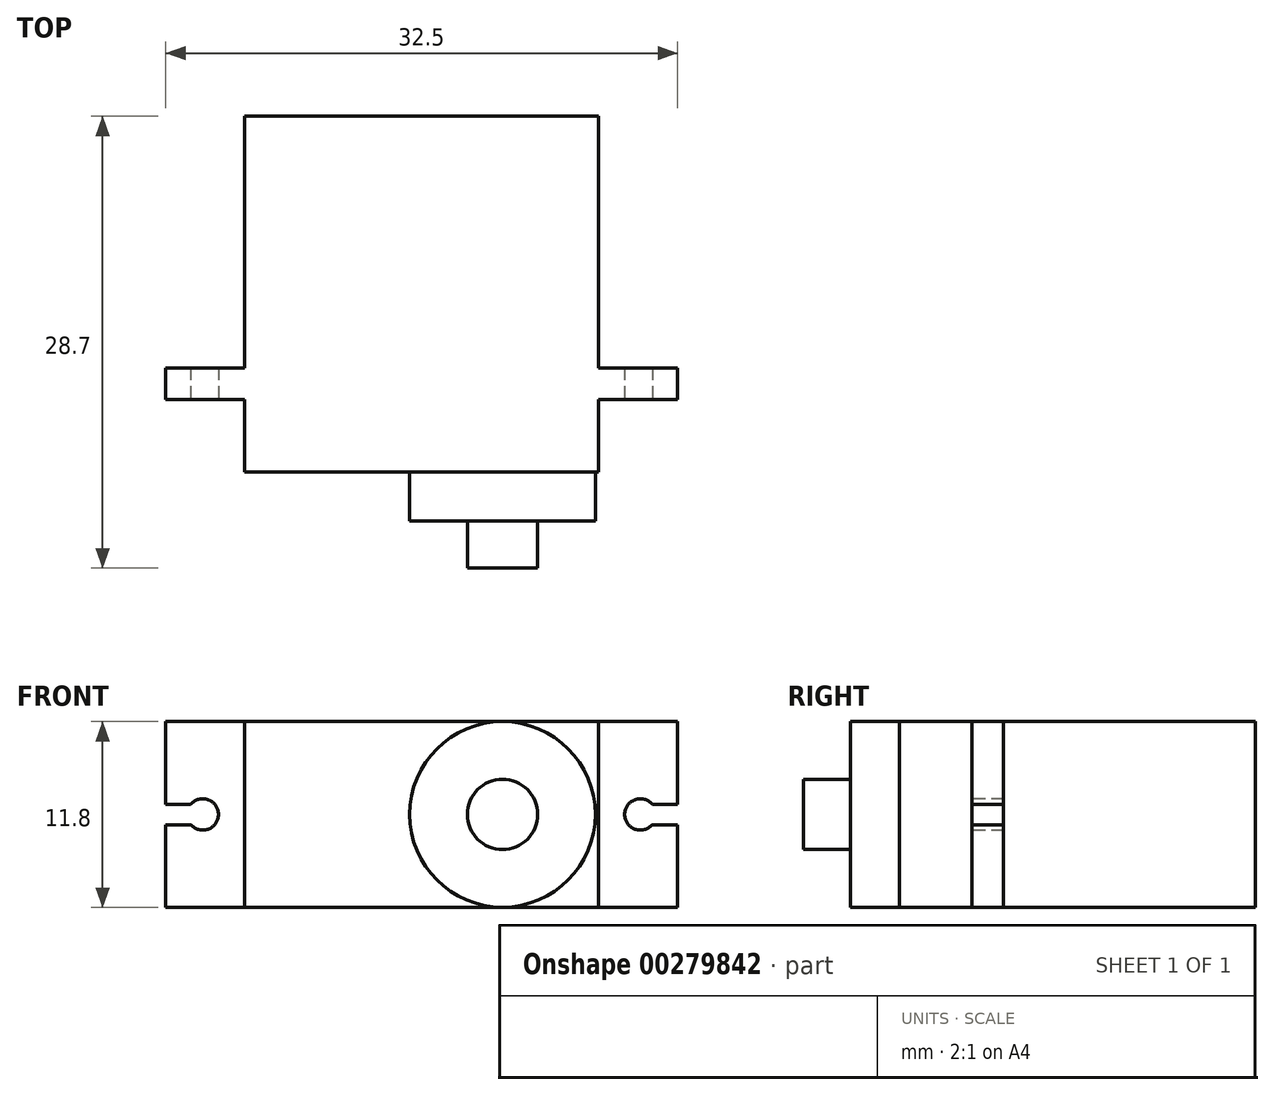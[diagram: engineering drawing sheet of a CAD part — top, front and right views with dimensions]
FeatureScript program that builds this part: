
annotation { "Feature Type Name" : "Feature", "Feature Type Description" : "" }
export const myFeature = defineFeature(function(context is Context, id is Id, definition is map)
    precondition{}
    {
        {
            var Q0;
            Q0=qCreatedBy(makeId("Front.planeOp"),FACE);
            var sketch = newSketch(context, id + "F0", { "sketchPlane" : qUnion([Q0])});
            skLineSegment(sketch, "E0.bottom", {"start": v(11.25, -5.9) * mm, "end": v(-11.25, -5.9) * mm});
            skLineSegment(sketch, "E0.top", {"start": v(11.25, 5.9) * mm, "end": v(-11.25, 5.9) * mm});
            skLineSegment(sketch, "E0.left", {"start": v(11.25, -5.9) * mm, "end": v(11.25, 5.9) * mm});
            skLineSegment(sketch, "E0.right", {"start": v(-11.25, -5.9) * mm, "end": v(-11.25, 5.9) * mm});
            skPoint(sketch, "E0.middle", {"position": v(0, 0) * mm});
            skSolve(sketch);
        }
        {
            var Q0;
            Q0 = qSketchRegion(id + "F0", true);
            extrude(context, id + "F1", {"entities" : qUnion([Q0]), "depth" : 22.6 * mm, "offsetDistance" : 25 * mm});
        }
        {
            var Q0;
            Q0=makeQuery(id+"F1.opExtrude","SWEPT_FACE",FACE,{"disambiguationData":[OSD([sQuery(id+"F0.wireOp",EDGE,"E0.right")])]});
            var sketch = newSketch(context, id + "F2", { "sketchPlane" : qUnion([Q0])});
            skLineSegment(sketch, "E1.bottom", {"start": v(18, 5.9) * mm, "end": v(16, 5.9) * mm});
            skLineSegment(sketch, "E1.top", {"start": v(18, -5.9) * mm, "end": v(16, -5.9) * mm});
            skLineSegment(sketch, "E1.left", {"start": v(18, 5.9) * mm, "end": v(18, -5.9) * mm});
            skLineSegment(sketch, "E1.right", {"start": v(16, 5.9) * mm, "end": v(16, -5.9) * mm});
            skSolve(sketch);
        }
        {
            var Q0;
            Q0 = qSketchRegion(id + "F2", true);
            extrude(context, id + "F3", {"entities" : qUnion([Q0]), "operationType" : NewBodyOperationType.ADD, "depth" : 5 * mm, "hasSecondDirection" : true, "secondDirectionOppositeDirection" : true, "secondDirectionDepth" : 27.5 * mm, "offsetDistance" : 25 * mm});
        }
        {
            var Q0;
            Q0=makeQuery(id+"F1.opExtrude","CAP_FACE",FACE,{"disambiguationData":[OSD([sQuery(id+"F0.wireOp",EDGE,"E0.bottom"),sQuery(id+"F0.wireOp",EDGE,"E0.top"),sQuery(id+"F0.wireOp",EDGE,"E0.left"),sQuery(id+"F0.wireOp",EDGE,"E0.right")])],"isStart":false});
            var sketch = newSketch(context, id + "F4", { "sketchPlane" : qUnion([Q0])});
            skCircle(sketch, "E2", {"center": v(5.14, 0) * mm, "radius": 5.9 * mm});
            skPoint(sketch, "E2.centerSnap0", {"position": v(11.25, 0) * mm});
            skSolve(sketch);
        }
        {
            var Q0;
            Q0 = qSketchRegion(id + "F4", true);
            extrude(context, id + "F5", {"entities" : qUnion([Q0]), "operationType" : NewBodyOperationType.ADD, "depth" : 3.1 * mm});
        }
        {
            var Q0;
            Q0=makeQuery(id+"F5.opExtrude","CAP_FACE",FACE,{"disambiguationData":[OSD([sQuery(id+"F4.wireOp",EDGE,"E2")])],"isStart":false});
            var sketch = newSketch(context, id + "F6", { "sketchPlane" : qUnion([Q0])});
            skCircle(sketch, "E3", {"center": v(5.14, 0) * mm, "radius": 2.23 * mm});
            skSolve(sketch);
        }
        {
            var Q0;
            Q0 = qSketchRegion(id + "F6", true);
            extrude(context, id + "F7", {"entities" : qUnion([Q0]), "operationType" : NewBodyOperationType.ADD, "depth" : 3 * mm, "offsetDistance" : 25 * mm});
        }
        {
            var Q0;
            {var subQ1=sQuery(id+"F2.wireOp",EDGE,"E1.left");Q0=makeQuery(id+"F3.boolean.opBoolean","SPLIT",FACE,{"disambiguationData":[TD([makeQuery(id+"F1.opExtrude","SWEPT_FACE",FACE,{"disambiguationData":[OSD([sQuery(id+"F0.wireOp",EDGE,"E0.right")])]})])],"derivedFrom":makeQuery(id+"F3.opExtrude","SWEPT_FACE",FACE,{"disambiguationData":[OSD([subQ1])]})});}
            var sketch = newSketch(context, id + "F8", { "sketchPlane" : qUnion([Q0])});
            skPoint(sketch, "E4", {"position": v(-13.9, 0) * mm});
            skPoint(sketch, "E5", {"position": v(13.9, 0) * mm});
            skSolve(sketch);
        }
        {
            var Q0;
            Q0=sQuery(id+"F8.wireOp",VERTEX,"E4");
            var Q1;
            Q1=sQuery(id+"F8.wireOp",VERTEX,"E5");
            var Q2;
            Q2=makeQuery(id+"F1.opExtrude","SWEPT_BODY",BODY,{"disambiguationData":[OSD([sQuery(id+"F0.wireOp",EDGE,"E0.bottom"),sQuery(id+"F0.wireOp",EDGE,"E0.top"),sQuery(id+"F0.wireOp",EDGE,"E0.left"),sQuery(id+"F0.wireOp",EDGE,"E0.right")])]});
            hole(context, id + "F9", {"style" : HoleStyle.SIMPLE, "endStyle" : HoleEndStyle.BLIND, "holeDiameter" : 2 * mm, "holeDepth" : 12 * mm, "tappedDepth" : 12 * mm, "tapClearance" : 3, "locations" : qUnion([Q0, Q1]), "scope" : qUnion([Q2])});
        }
        {
            var Q0;
            {var subQ1=sQuery(id+"F2.wireOp",EDGE,"E1.left");Q0=makeQuery(id+"F3.boolean.opBoolean","SPLIT",FACE,{"disambiguationData":[TD([makeQuery(id+"F1.opExtrude","SWEPT_FACE",FACE,{"disambiguationData":[OSD([sQuery(id+"F0.wireOp",EDGE,"E0.right")])]})])],"derivedFrom":makeQuery(id+"F3.opExtrude","SWEPT_FACE",FACE,{"disambiguationData":[OSD([subQ1])]})});}
            var sketch = newSketch(context, id + "F10", { "sketchPlane" : qUnion([Q0])});
            skLineSegment(sketch, "E6.bottom", {"start": v(-13.93, 0.65) * mm, "end": v(-23.32, 0.65) * mm});
            skLineSegment(sketch, "E6.top", {"start": v(-13.93, -0.65) * mm, "end": v(-23.32, -0.65) * mm});
            skLineSegment(sketch, "E6.left", {"start": v(-13.93, 0.65) * mm, "end": v(-13.93, -0.65) * mm});
            skLineSegment(sketch, "E6.right", {"start": v(-23.32, 0.65) * mm, "end": v(-23.32, -0.65) * mm});
            skPoint(sketch, "E6.middle", {"position": v(-18.62, 0) * mm});
            skLineSegment(sketch, "E7.bottom", {"start": v(23.46, 0.65) * mm, "end": v(14.07, 0.65) * mm});
            skLineSegment(sketch, "E7.top", {"start": v(23.46, -0.65) * mm, "end": v(14.07, -0.65) * mm});
            skLineSegment(sketch, "E7.left", {"start": v(23.46, 0.65) * mm, "end": v(23.46, -0.65) * mm});
            skLineSegment(sketch, "E7.right", {"start": v(14.07, 0.65) * mm, "end": v(14.07, -0.65) * mm});
            skPoint(sketch, "E7.middle", {"position": v(18.76, 0) * mm});
            skSolve(sketch);
        }
        {
            var Q0;
            {var subQ0=sQuery(id+"F10.wireOp",EDGE,"E6.right");Q0=makeQuery(id+"F10.imprint","IMPRINT",FACE,{"disambiguationData":[TD([[makeQuery(id+"F10.imprint","IMPRINT",EDGE,{"derivedFrom":subQ0}),1.0]])]});}
            var Q1;
            {var subQ0=sQuery(id+"F10.wireOp",EDGE,"E6.bottom");var subQ1=makeQuery(id+"F3.opExtrude","CAP_EDGE",EDGE,{"disambiguationData":[OSD([sQuery(id+"F2.wireOp",EDGE,"E1.left")])],"isStart":false});var subQ2=makeQuery(id+"F10.imprint","INTERSECT",VERTEX,{"derivedFrom":[subQ1,subQ0]});Q1=makeQuery(id+"F10.imprint","IMPRINT",FACE,{"disambiguationData":[TD([[makeQuery(id+"F10.imprint","IMPRINT",EDGE,{"disambiguationData":[TD([[subQ2,-1.0]])],"derivedFrom":subQ1}),1.0]])]});}
            var Q2;
            {var subQ0=sQuery(id+"F10.wireOp",EDGE,"E6.left");Q2=makeQuery(id+"F10.imprint","IMPRINT",FACE,{"disambiguationData":[TD([[makeQuery(id+"F10.imprint","IMPRINT",EDGE,{"derivedFrom":subQ0}),-1.0]])]});}
            var Q3;
            Q3=makeQuery(id+"F10.imprint","IMPRINT",FACE,{"disambiguationData":[TD([[makeQuery(id+"F10.imprint","IMPRINT",EDGE,{"derivedFrom":sQuery(id+"F10.wireOp",EDGE,"E7.bottom")}),1.0]])]});
            extrude(context, id + "F11", {"entities" : qUnion([Q0, Q1, Q2, Q3]), "operationType" : NewBodyOperationType.REMOVE, "oppositeDirection" : true, "depth" : 5 * mm});
        }
    });
